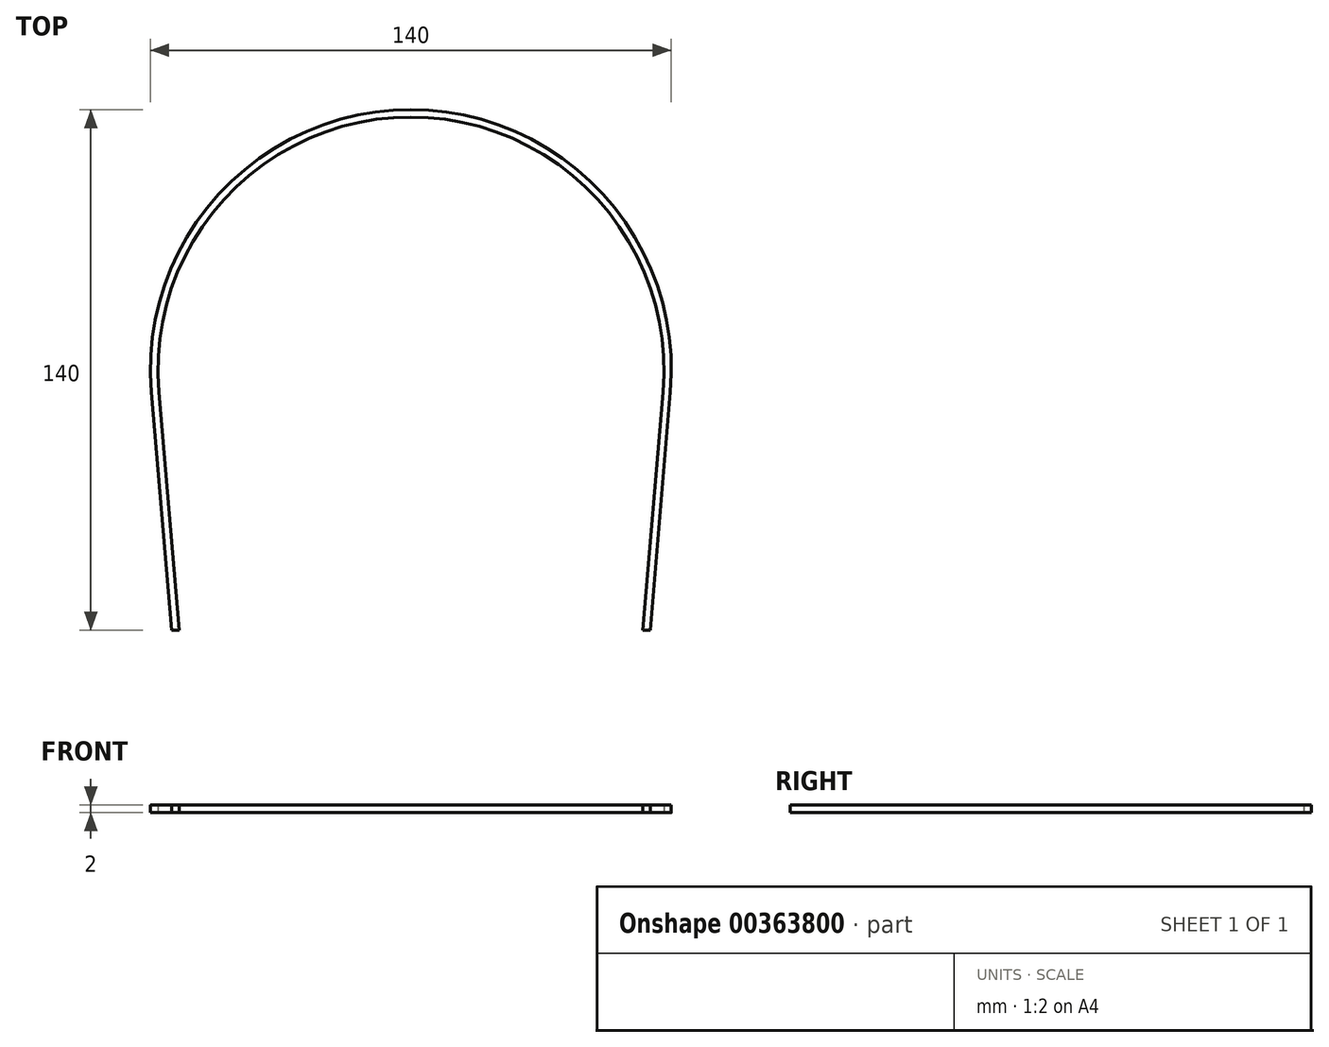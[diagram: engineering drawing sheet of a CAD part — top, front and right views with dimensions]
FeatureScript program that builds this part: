
annotation { "Feature Type Name" : "Feature", "Feature Type Description" : "" }
export const myFeature = defineFeature(function(context is Context, id is Id, definition is map)
    precondition{}
    {
        {
            var Q0;
            Q0=qCreatedBy(makeId("Top.planeOp"),FACE);
            var sketch = newSketch(context, id + "F0", { "sketchPlane" : qUnion([Q0])});
            skArc(sketch, "E0", {"start": v(69.75, -5.92) * mm, "mid": v(0, 70) * mm, "end": v(-69.75, -5.92) * mm});
            skArc(sketch, "E1", {"start": v(67.74, -5.92) * mm, "mid": v(0, 68) * mm, "end": v(-67.74, -5.92) * mm});
            skLineSegment(sketch, "E2", {"start": v(-69.75, -5.92) * mm, "end": v(-64.31, -70) * mm});
            skLineSegment(sketch, "E3", {"start": v(-67.74, -5.92) * mm, "end": v(-62.3, -70) * mm});
            skLineSegment(sketch, "E4", {"start": v(-64.31, -70) * mm, "end": v(-62.3, -70) * mm});
            skLineSegment(sketch, "E5.MirrorCS", {"start": v(69.75, -5.92) * mm, "end": v(64.31, -70) * mm});
            skLineSegment(sketch, "E6.MirrorCS", {"start": v(67.74, -5.92) * mm, "end": v(62.3, -70) * mm});
            skLineSegment(sketch, "E7.MirrorCS", {"start": v(64.31, -70) * mm, "end": v(62.3, -70) * mm});
            skSolve(sketch);
        }
        {
            var Q0;
            Q0 = qSketchRegion(id + "F0", true);
            extrude(context, id + "F1", {"entities" : qUnion([Q0]), "depth" : 2 * mm});
        }
    });
